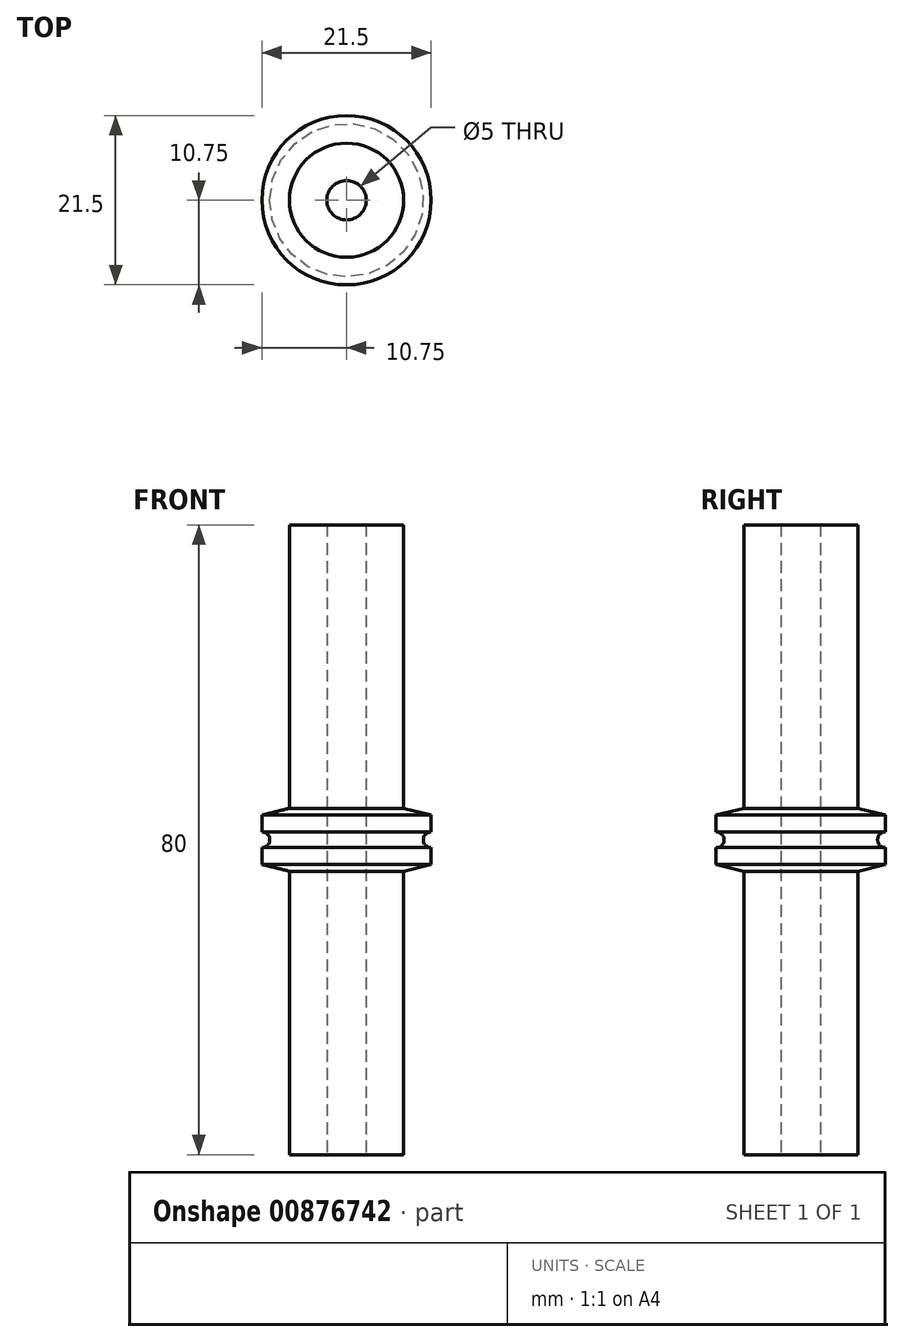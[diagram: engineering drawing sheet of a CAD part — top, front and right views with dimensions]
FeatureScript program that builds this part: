
annotation { "Feature Type Name" : "Feature", "Feature Type Description" : "" }
export const myFeature = defineFeature(function(context is Context, id is Id, definition is map)
    precondition{}
    {
        {
            var Q0;
            Q0=qCreatedBy(makeId("Top.planeOp"),FACE);
            var sketch = newSketch(context, id + "F0", { "sketchPlane" : qUnion([Q0])});
            skCircle(sketch, "E0", {"center": v(0, 0) * mm, "radius": 7.25 * mm});
            skCircle(sketch, "E1", {"center": v(0, 0) * mm, "radius": 2.5 * mm});
            skSolve(sketch);
        }
        {
            var Q0;
            Q0 = qSketchRegion(id + "F0", true);
            extrude(context, id + "F1", {"entities" : qUnion([Q0]), "depth" : 40 * mm, "offsetDistance" : 25 * mm});
        }
        {
            var Q0;
            Q0=qCreatedBy(makeId("Front.planeOp"),FACE);
            var sketch = newSketch(context, id + "F2", { "sketchPlane" : qUnion([Q0])});
            skLineSegment(sketch, "E2", {"start": v(0, 0) * mm, "end": v(0, 3) * mm, "construction": true});
            skLineSegment(sketch, "E3", {"start": v(2.5, 3) * mm, "end": v(10.75, 3) * mm});
            skLineSegment(sketch, "E4", {"start": v(10.75, 3) * mm, "end": v(10.75, 1) * mm});
            skLineSegment(sketch, "E5", {"start": v(9.75, 0) * mm, "end": v(2.5, 0) * mm});
            skArc(sketch, "E6", {"start": v(10.75, 1) * mm, "mid": v(10.04, 0.7) * mm, "end": v(9.75, 0) * mm});
            skLineSegment(sketch, "E7", {"start": v(2.5, 0) * mm, "end": v(2.5, 3) * mm});
            skSolve(sketch);
        }
        {
            var Q0;
            Q0 = qSketchRegion(id + "F2", true);
            var Q1;
            Q1=sQuery(id+"F2.wireOp",EDGE,"E2");
            revolve(context, id + "F3", {"operationType" : NewBodyOperationType.ADD, "surfaceOperationType" : NewSurfaceOperationType.NEW, "entities" : qUnion([Q0]), "axis" : qUnion([Q1]), "revolveType" : RevolveType.FULL});
        }
        {
            var Q0;
            Q0=makeQuery(id+"F3.boolean.opBoolean","INTERSECT",EDGE,{"derivedFrom":[makeQuery(id+"F1.opExtrude","SWEPT_FACE",FACE,{"disambiguationData":[OSD([sQuery(id+"F0.wireOp",EDGE,"E0")])]}),makeQuery(id+"F3.opRevolve","SWEPT_FACE",FACE,{"disambiguationData":[OSD([sQuery(id+"F2.wireOp",EDGE,"E3")])]})]});
            chamfer(context, id + "F4", {"entities" : qUnion([Q0]), "chamferType" : ChamferType.TWO_OFFSETS, "width1" : 4 * mm, "oppositeDirection" : false, "width2" : 1 * mm, "tangentPropagation" : true});
        }
        {
            var Q0;
            Q0=makeQuery(id+"F1.opExtrude","SWEPT_BODY",BODY,{"disambiguationData":[OSD([sQuery(id+"F0.wireOp",EDGE,"E0"),sQuery(id+"F0.wireOp",EDGE,"E1")])]});
            var Q1;
            Q1=makeQuery(id+"F3.boolean.opBoolean","MERGE",FACE,{"derivedFrom":[makeQuery(id+"F1.opExtrude","CAP_FACE",FACE,{"disambiguationData":[OSD([sQuery(id+"F0.wireOp",EDGE,"E0"),sQuery(id+"F0.wireOp",EDGE,"E1")])],"isStart":true}),makeQuery(id+"F3.opRevolve","SWEPT_FACE",FACE,{"disambiguationData":[OSD([sQuery(id+"F2.wireOp",EDGE,"E5")])]})]});
            mirror(context, id + "F5", {"operationType" : NewBodyOperationType.ADD, "entities" : qUnion([Q0]), "mirrorPlane" : qUnion([Q1])});
        }
    });
